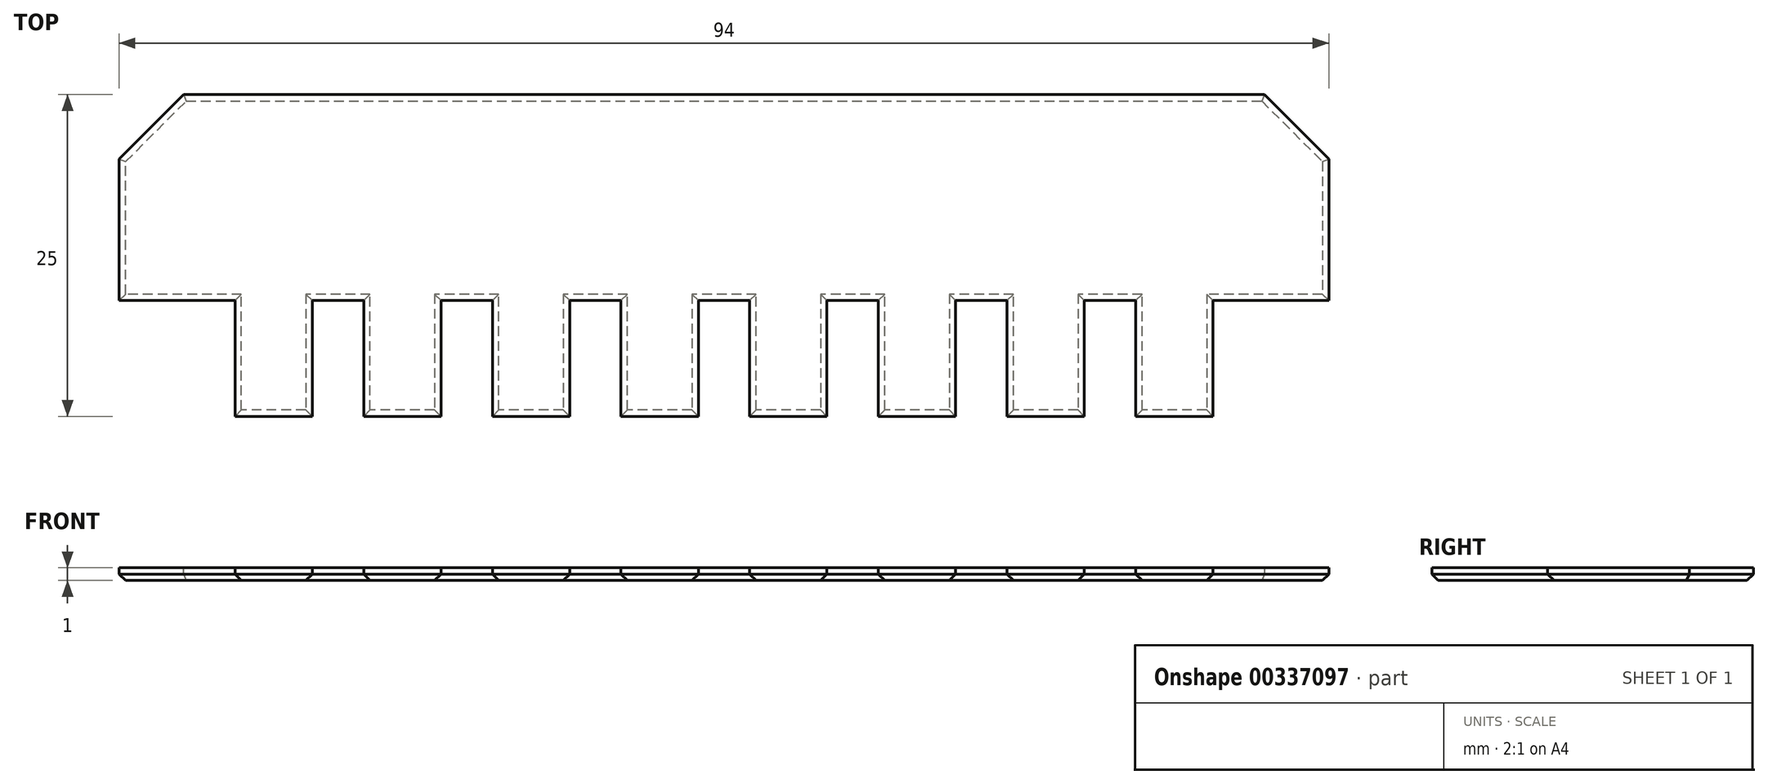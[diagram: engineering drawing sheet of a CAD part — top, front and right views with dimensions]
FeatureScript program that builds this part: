
annotation { "Feature Type Name" : "Feature", "Feature Type Description" : "" }
export const myFeature = defineFeature(function(context is Context, id is Id, definition is map)
    precondition{}
    {
        {
            var Q0;
            Q0=qCreatedBy(makeId("Top.planeOp"),FACE);
            var sketch = newSketch(context, id + "F0", { "sketchPlane" : qUnion([Q0])});
            skLineSegment(sketch, "E0.bottom", {"start": v(47, -12.5) * mm, "end": v(-47, -12.5) * mm});
            skLineSegment(sketch, "E0.top", {"start": v(47, 12.5) * mm, "end": v(-47, 12.5) * mm});
            skLineSegment(sketch, "E0.left", {"start": v(47, -12.5) * mm, "end": v(47, 12.5) * mm});
            skLineSegment(sketch, "E0.right", {"start": v(-47, -12.5) * mm, "end": v(-47, 12.5) * mm});
            skPoint(sketch, "E0.middle", {"position": v(0, 0) * mm});
            skSolve(sketch);
        }
        {
            var Q0;
            Q0=makeQuery(id+"F0.imprint","IMPRINT",FACE,{"disambiguationData":[TD([[makeQuery(id+"F0.imprint","IMPRINT",EDGE,{"derivedFrom":sQuery(id+"F0.wireOp",EDGE,"E0.bottom")}),-1.0]])]});
            var sketch = newSketch(context, id + "F1", { "sketchPlane" : qUnion([Q0])});
            skLineSegment(sketch, "E1.bottom", {"start": v(-47, -3.5) * mm, "end": v(-38, -3.5) * mm});
            skLineSegment(sketch, "E1.top", {"start": v(-47, -12.5) * mm, "end": v(-38, -12.5) * mm, "construction": true});
            skLineSegment(sketch, "E1.left", {"start": v(-47, -3.5) * mm, "end": v(-47, -12.5) * mm, "construction": true});
            skLineSegment(sketch, "E1.right", {"start": v(-38, -3.5) * mm, "end": v(-38, -12.5) * mm});
            skLineSegment(sketch, "E2", {"start": v(0, 28.55) * mm, "end": v(0, -32.57) * mm, "construction": true});
            skLineSegment(sketch, "E3.MirrorCS", {"start": v(47, -3.5) * mm, "end": v(38, -3.5) * mm});
            skLineSegment(sketch, "E4.MirrorCS", {"start": v(38, -3.5) * mm, "end": v(38, -12.5) * mm});
            skLineSegment(sketch, "E5.MirrorCS", {"start": v(47, -3.5) * mm, "end": v(47, -12.5) * mm, "construction": true});
            skLineSegment(sketch, "E6.MirrorCS", {"start": v(47, -12.5) * mm, "end": v(38, -12.5) * mm, "construction": true});
            skLineSegment(sketch, "E7", {"start": v(-32, -3.5) * mm, "end": v(-28, -3.5) * mm, "construction": true});
            skLineSegment(sketch, "E8.top", {"start": v(-38, -12.5) * mm, "end": v(-32, -12.5) * mm});
            skLineSegment(sketch, "E8.right", {"start": v(-32, -3.5) * mm, "end": v(-32, -12.5) * mm});
            skLineSegment(sketch, "E9.top", {"start": v(-28, -12.5) * mm, "end": v(-22, -12.5) * mm});
            skLineSegment(sketch, "E9.left", {"start": v(-28, -3.5) * mm, "end": v(-28, -12.5) * mm});
            skLineSegment(sketch, "E9.right", {"start": v(-22, -3.5) * mm, "end": v(-22, -12.5) * mm});
            skLineSegment(sketch, "E10", {"start": v(-32, -3.5) * mm, "end": v(-28, -3.5) * mm});
            skLineSegment(sketch, "E11.trimOffspring", {"start": v(-22, -3.5) * mm, "end": v(38, -3.5) * mm, "construction": true});
            skLineSegment(sketch, "E12", {"start": v(-22, -8) * mm, "end": v(-20, -8) * mm, "construction": true});
            skLineSegment(sketch, "E13", {"start": v(-20, -8) * mm, "end": v(-20, 6.94) * mm, "construction": true});
            skLineSegment(sketch, "E14.MirrorCS", {"start": v(-2, -3.5) * mm, "end": v(-2, -12.5) * mm});
            skLineSegment(sketch, "E15.MirrorCS", {"start": v(-2, -12.5) * mm, "end": v(-8, -12.5) * mm});
            skLineSegment(sketch, "E16.MirrorCS", {"start": v(-8, -3.5) * mm, "end": v(-8, -12.5) * mm});
            skLineSegment(sketch, "E17.MirrorCS", {"start": v(-8, -3.5) * mm, "end": v(-12, -3.5) * mm, "construction": true});
            skLineSegment(sketch, "E18.MirrorCS", {"start": v(-12, -3.5) * mm, "end": v(-12, -12.5) * mm});
            skLineSegment(sketch, "E19.MirrorCS", {"start": v(-12, -12.5) * mm, "end": v(-18, -12.5) * mm});
            skLineSegment(sketch, "E20.MirrorCS", {"start": v(-18, -3.5) * mm, "end": v(-18, -12.5) * mm});
            skLineSegment(sketch, "E21", {"start": v(-22, -3.5) * mm, "end": v(-18, -3.5) * mm});
            skLineSegment(sketch, "E22.MirrorCS", {"start": v(38, -12.5) * mm, "end": v(32, -12.5) * mm});
            skLineSegment(sketch, "E23.MirrorCS", {"start": v(32, -3.5) * mm, "end": v(32, -12.5) * mm});
            skLineSegment(sketch, "E24.MirrorCS", {"start": v(32, -3.5) * mm, "end": v(28, -3.5) * mm, "construction": true});
            skLineSegment(sketch, "E25.MirrorCS", {"start": v(28, -3.5) * mm, "end": v(28, -12.5) * mm});
            skLineSegment(sketch, "E26.MirrorCS", {"start": v(28, -12.5) * mm, "end": v(22, -12.5) * mm});
            skLineSegment(sketch, "E27.MirrorCS", {"start": v(22, -3.5) * mm, "end": v(22, -12.5) * mm});
            skLineSegment(sketch, "E28.MirrorCS", {"start": v(18, -3.5) * mm, "end": v(18, -12.5) * mm});
            skLineSegment(sketch, "E29.MirrorCS", {"start": v(12, -12.5) * mm, "end": v(18, -12.5) * mm});
            skLineSegment(sketch, "E30.MirrorCS", {"start": v(12, -3.5) * mm, "end": v(12, -12.5) * mm});
            skLineSegment(sketch, "E31.MirrorCS", {"start": v(8, -3.5) * mm, "end": v(8, -12.5) * mm});
            skLineSegment(sketch, "E32.MirrorCS", {"start": v(2, -12.5) * mm, "end": v(8, -12.5) * mm});
            skLineSegment(sketch, "E33.MirrorCS", {"start": v(2, -3.5) * mm, "end": v(2, -12.5) * mm});
            skLineSegment(sketch, "E34", {"start": v(-12, -3.5) * mm, "end": v(-8, -3.5) * mm});
            skLineSegment(sketch, "E35", {"start": v(-2, -3.5) * mm, "end": v(2, -3.5) * mm});
            skLineSegment(sketch, "E36", {"start": v(8, -3.5) * mm, "end": v(12, -3.5) * mm});
            skLineSegment(sketch, "E37", {"start": v(18, -3.5) * mm, "end": v(22, -3.5) * mm});
            skLineSegment(sketch, "E38", {"start": v(-47, -3.5) * mm, "end": v(-47, 12.5) * mm});
            skLineSegment(sketch, "E39", {"start": v(-47, 12.5) * mm, "end": v(47, 12.5) * mm});
            skLineSegment(sketch, "E40", {"start": v(47, 12.5) * mm, "end": v(47, -3.5) * mm});
            skLineSegment(sketch, "E41", {"start": v(28, -3.5) * mm, "end": v(32, -3.5) * mm});
            skSolve(sketch);
        }
        {
            var Q0;
            Q0 = qSketchRegion(id + "F1", true);
            extrude(context, id + "F2", {"entities" : qUnion([Q0]), "depth" : 1 * mm});
        }
        {
            var Q0;
            Q0=makeQuery(id+"F2.opExtrude","SWEPT_EDGE",EDGE,{"disambiguationData":[OSD([sQuery(id+"F1.wireOp",EDGE,"E39"),sQuery(id+"F1.wireOp",EDGE,"E40")])]});
            var Q1;
            Q1=makeQuery(id+"F2.opExtrude","SWEPT_EDGE",EDGE,{"disambiguationData":[OSD([sQuery(id+"F1.wireOp",EDGE,"E38"),sQuery(id+"F1.wireOp",EDGE,"E39")])]});
            chamfer(context, id + "F3", {"entities" : qUnion([Q0, Q1]), "width" : 5 * mm, "tangentPropagation" : true});
        }
        {
            var Q0;
            Q0=makeQuery(id+"F2.opExtrude","CAP_FACE",FACE,{"disambiguationData":[OSD([sQuery(id+"F1.wireOp",EDGE,"E1.bottom"),sQuery(id+"F1.wireOp",EDGE,"E3.MirrorCS"),sQuery(id+"F1.wireOp",EDGE,"E8.top"),sQuery(id+"F1.wireOp",EDGE,"E1.right"),sQuery(id+"F1.wireOp",EDGE,"E8.right"),sQuery(id+"F1.wireOp",EDGE,"E9.top"),sQuery(id+"F1.wireOp",EDGE,"E9.left"),sQuery(id+"F1.wireOp",EDGE,"E9.right"),sQuery(id+"F1.wireOp",EDGE,"E10"),sQuery(id+"F1.wireOp",EDGE,"E14.MirrorCS"),sQuery(id+"F1.wireOp",EDGE,"E15.MirrorCS"),sQuery(id+"F1.wireOp",EDGE,"E16.MirrorCS"),sQuery(id+"F1.wireOp",EDGE,"E18.MirrorCS"),sQuery(id+"F1.wireOp",EDGE,"E19.MirrorCS"),sQuery(id+"F1.wireOp",EDGE,"E20.MirrorCS"),sQuery(id+"F1.wireOp",EDGE,"E21"),sQuery(id+"F1.wireOp",EDGE,"E4.MirrorCS"),sQuery(id+"F1.wireOp",EDGE,"E22.MirrorCS"),sQuery(id+"F1.wireOp",EDGE,"E23.MirrorCS"),sQuery(id+"F1.wireOp",EDGE,"E25.MirrorCS"),sQuery(id+"F1.wireOp",EDGE,"E26.MirrorCS"),sQuery(id+"F1.wireOp",EDGE,"E27.MirrorCS"),sQuery(id+"F1.wireOp",EDGE,"E28.MirrorCS"),sQuery(id+"F1.wireOp",EDGE,"E29.MirrorCS"),sQuery(id+"F1.wireOp",EDGE,"E30.MirrorCS"),sQuery(id+"F1.wireOp",EDGE,"E31.MirrorCS"),sQuery(id+"F1.wireOp",EDGE,"E32.MirrorCS"),sQuery(id+"F1.wireOp",EDGE,"E33.MirrorCS"),sQuery(id+"F1.wireOp",EDGE,"E34"),sQuery(id+"F1.wireOp",EDGE,"E35"),sQuery(id+"F1.wireOp",EDGE,"E36"),sQuery(id+"F1.wireOp",EDGE,"E37"),sQuery(id+"F1.wireOp",EDGE,"E38"),sQuery(id+"F1.wireOp",EDGE,"E39"),sQuery(id+"F1.wireOp",EDGE,"E40"),sQuery(id+"F1.wireOp",EDGE,"E41")])],"isStart":true});
            chamfer(context, id + "F4", {"entities" : qUnion([Q0]), "width" : 0.5 * mm, "tangentPropagation" : true});
        }
    });
